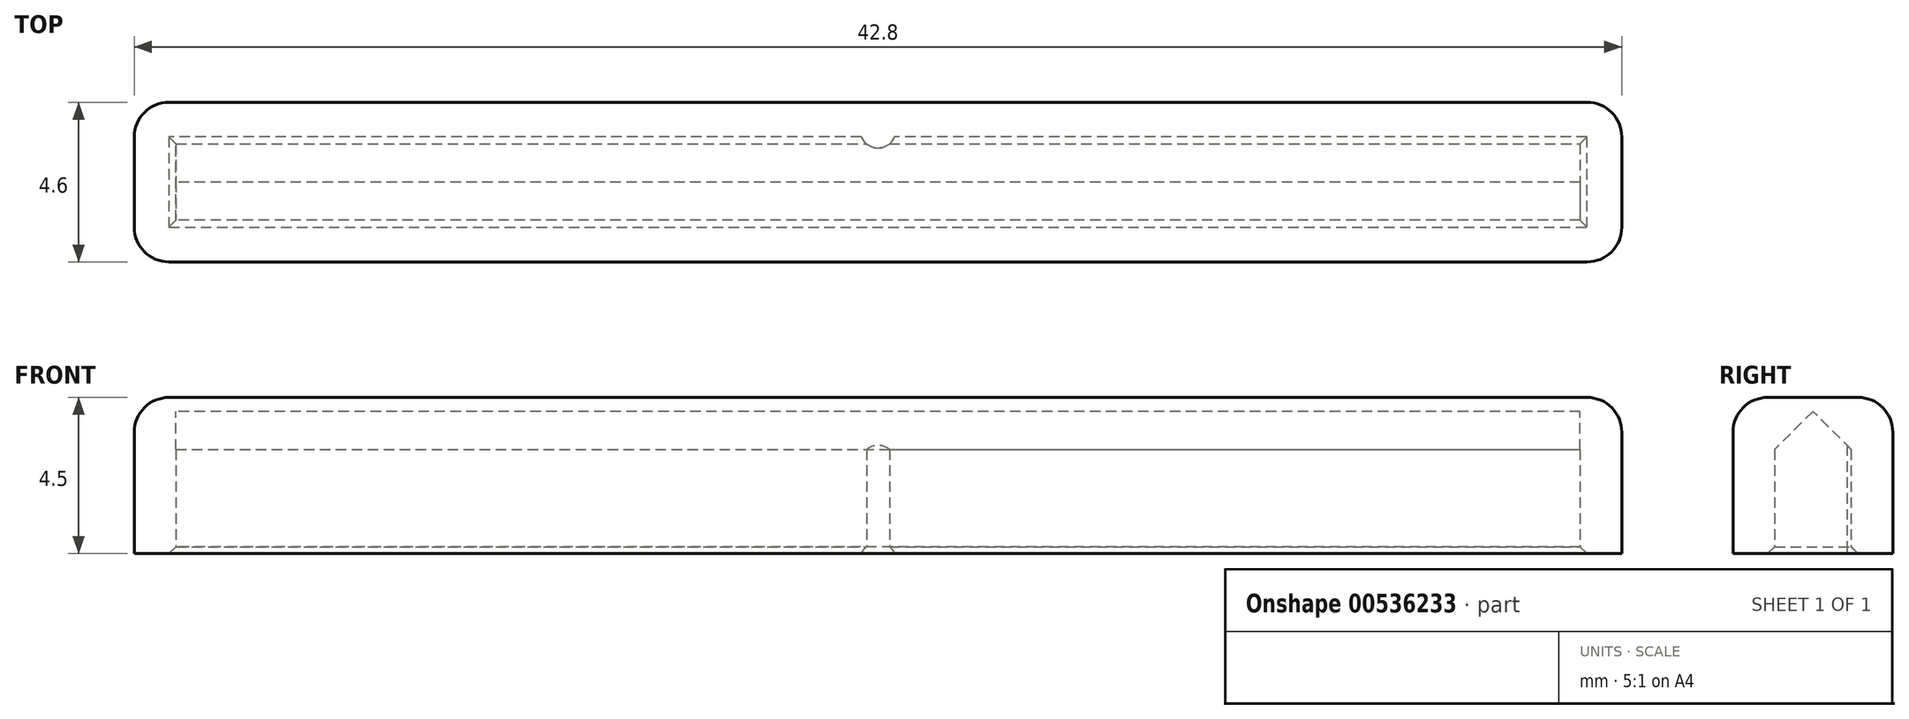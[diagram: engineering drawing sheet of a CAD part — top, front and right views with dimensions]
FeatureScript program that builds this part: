
annotation { "Feature Type Name" : "Feature", "Feature Type Description" : "" }
export const myFeature = defineFeature(function(context is Context, id is Id, definition is map)
    precondition{}
    {
        {
            var Q0;
            Q0=qCreatedBy(makeId("Top.planeOp"),FACE);
            var sketch = newSketch(context, id + "F0", { "sketchPlane" : qUnion([Q0])});
            skLineSegment(sketch, "E0.bottom", {"start": v(-20.2, 1.1) * mm, "end": v(20.2, 1.1) * mm});
            skLineSegment(sketch, "E0.top", {"start": v(-20.2, -1.1) * mm, "end": v(20.2, -1.1) * mm});
            skLineSegment(sketch, "E0.left", {"start": v(-20.2, 1.1) * mm, "end": v(-20.2, -1.1) * mm});
            skLineSegment(sketch, "E0.right", {"start": v(20.2, 1.1) * mm, "end": v(20.2, -1.1) * mm});
            skLineSegment(sketch, "E1.bottom", {"start": v(-21.4, 2.3) * mm, "end": v(21.4, 2.3) * mm});
            skLineSegment(sketch, "E1.top", {"start": v(-21.4, -2.3) * mm, "end": v(21.4, -2.3) * mm});
            skLineSegment(sketch, "E1.left", {"start": v(-21.4, 2.3) * mm, "end": v(-21.4, -2.3) * mm});
            skLineSegment(sketch, "E1.right", {"start": v(21.4, 2.3) * mm, "end": v(21.4, -2.3) * mm});
            skSolve(sketch);
        }
        {
            var Q0;
            Q0 = qSketchRegion(id + "F0", true);
            extrude(context, id + "F1", {"entities" : qUnion([Q0]), "depth" : 3 * mm, "offsetDistance" : 25 * mm});
        }
        {
            var Q0;
            Q0=makeQuery(id+"F1.opExtrude","CAP_FACE",FACE,{"disambiguationData":[OSD([sQuery(id+"F0.wireOp",EDGE,"E0.bottom"),sQuery(id+"F0.wireOp",EDGE,"E0.top"),sQuery(id+"F0.wireOp",EDGE,"E0.left"),sQuery(id+"F0.wireOp",EDGE,"E0.right"),sQuery(id+"F0.wireOp",EDGE,"E1.bottom"),sQuery(id+"F0.wireOp",EDGE,"E1.top"),sQuery(id+"F0.wireOp",EDGE,"E1.left"),sQuery(id+"F0.wireOp",EDGE,"E1.right")])],"isStart":false});
            var sketch = newSketch(context, id + "F2", { "sketchPlane" : qUnion([Q0])});
            skLineSegment(sketch, "E2.bottom", {"start": v(-21.4, 2.3) * mm, "end": v(21.4, 2.3) * mm});
            skLineSegment(sketch, "E2.top", {"start": v(-21.4, -2.3) * mm, "end": v(21.4, -2.3) * mm});
            skLineSegment(sketch, "E2.left", {"start": v(-21.4, 2.3) * mm, "end": v(-21.4, -2.3) * mm});
            skLineSegment(sketch, "E2.right", {"start": v(21.4, 2.3) * mm, "end": v(21.4, -2.3) * mm});
            skSolve(sketch);
        }
        {
            var Q0;
            Q0 = qSketchRegion(id + "F2", true);
            extrude(context, id + "F3", {"entities" : qUnion([Q0]), "operationType" : NewBodyOperationType.ADD, "depth" : 1.5 * mm, "offsetDistance" : 25 * mm});
        }
        {
            var Q0;
            Q0=makeQuery(id+"F1.opExtrude","SWEPT_FACE",FACE,{"disambiguationData":[OSD([sQuery(id+"F0.wireOp",EDGE,"E0.left")])]});
            var sketch = newSketch(context, id + "F4", { "sketchPlane" : qUnion([Q0])});
            skLineSegment(sketch, "E3", {"start": v(1.1, 3) * mm, "end": v(0, 4.1) * mm});
            skLineSegment(sketch, "E4", {"start": v(0, 4.1) * mm, "end": v(-1.1, 3) * mm});
            skLineSegment(sketch, "E5", {"start": v(-1.1, 3) * mm, "end": v(1.1, 3) * mm});
            skSolve(sketch);
        }
        {
            var Q0;
            Q0 = qSketchRegion(id + "F4", true);
            var Q1;
            Q1=makeQuery(id+"F1.opExtrude","SWEPT_FACE",FACE,{"disambiguationData":[OSD([sQuery(id+"F0.wireOp",EDGE,"E0.right")])]});
            extrude(context, id + "F5", {"entities" : qUnion([Q0]), "operationType" : NewBodyOperationType.REMOVE, "endBound" : BoundingType.UP_TO_SURFACE, "depth" : 10 * mm, "endBoundEntityFace" : qUnion([Q1]), "offsetDistance" : 25 * mm});
        }
        {
            var Q0;
            Q0=makeQuery(id+"F1.opExtrude","CAP_EDGE",EDGE,{"disambiguationData":[OSD([sQuery(id+"F0.wireOp",EDGE,"E0.bottom")])],"isStart":true});
            var Q1;
            Q1=makeQuery(id+"F1.opExtrude","CAP_EDGE",EDGE,{"disambiguationData":[OSD([sQuery(id+"F0.wireOp",EDGE,"E0.left")])],"isStart":true});
            var Q2;
            Q2=makeQuery(id+"F1.opExtrude","CAP_EDGE",EDGE,{"disambiguationData":[OSD([sQuery(id+"F0.wireOp",EDGE,"E0.top")])],"isStart":true});
            var Q3;
            Q3=makeQuery(id+"F1.opExtrude","CAP_EDGE",EDGE,{"disambiguationData":[OSD([sQuery(id+"F0.wireOp",EDGE,"E0.right")])],"isStart":true});
            chamfer(context, id + "F6", {"entities" : qUnion([Q0, Q1, Q2, Q3]), "width" : 0.2 * mm, "tangentPropagation" : true});
        }
        {
            var Q0;
            Q0=makeQuery(id+"F3.boolean.opBoolean","MERGE",EDGE,{"derivedFrom":[makeQuery(id+"F1.opExtrude","SWEPT_EDGE",EDGE,{"disambiguationData":[OSD([sQuery(id+"F0.wireOp",EDGE,"E1.top"),sQuery(id+"F0.wireOp",EDGE,"E1.left")])]}),makeQuery(id+"F3.opExtrude","SWEPT_EDGE",EDGE,{"disambiguationData":[OSD([sQuery(id+"F2.wireOp",EDGE,"E2.top"),sQuery(id+"F2.wireOp",EDGE,"E2.left")])]})]});
            var Q1;
            Q1=makeQuery(id+"F3.boolean.opBoolean","MERGE",EDGE,{"derivedFrom":[makeQuery(id+"F1.opExtrude","SWEPT_EDGE",EDGE,{"disambiguationData":[OSD([sQuery(id+"F0.wireOp",EDGE,"E1.bottom"),sQuery(id+"F0.wireOp",EDGE,"E1.left")])]}),makeQuery(id+"F3.opExtrude","SWEPT_EDGE",EDGE,{"disambiguationData":[OSD([sQuery(id+"F2.wireOp",EDGE,"E2.bottom"),sQuery(id+"F2.wireOp",EDGE,"E2.left")])]})]});
            var Q2;
            Q2=makeQuery(id+"F3.opExtrude","CAP_EDGE",EDGE,{"disambiguationData":[OSD([sQuery(id+"F2.wireOp",EDGE,"E2.left")])],"isStart":false});
            var Q3;
            Q3=makeQuery(id+"F3.opExtrude","CAP_EDGE",EDGE,{"disambiguationData":[OSD([sQuery(id+"F2.wireOp",EDGE,"E2.bottom")])],"isStart":false});
            var Q4;
            Q4=makeQuery(id+"F3.opExtrude","CAP_EDGE",EDGE,{"disambiguationData":[OSD([sQuery(id+"F2.wireOp",EDGE,"E2.top")])],"isStart":false});
            var Q5;
            Q5=makeQuery(id+"F3.boolean.opBoolean","MERGE",EDGE,{"derivedFrom":[makeQuery(id+"F1.opExtrude","SWEPT_EDGE",EDGE,{"disambiguationData":[OSD([sQuery(id+"F0.wireOp",EDGE,"E1.top"),sQuery(id+"F0.wireOp",EDGE,"E1.right")])]}),makeQuery(id+"F3.opExtrude","SWEPT_EDGE",EDGE,{"disambiguationData":[OSD([sQuery(id+"F2.wireOp",EDGE,"E2.top"),sQuery(id+"F2.wireOp",EDGE,"E2.right")])]})]});
            var Q6;
            Q6=makeQuery(id+"F3.opExtrude","CAP_EDGE",EDGE,{"disambiguationData":[OSD([sQuery(id+"F2.wireOp",EDGE,"E2.right")])],"isStart":false});
            var Q7;
            Q7=makeQuery(id+"F3.boolean.opBoolean","MERGE",EDGE,{"derivedFrom":[makeQuery(id+"F1.opExtrude","SWEPT_EDGE",EDGE,{"disambiguationData":[OSD([sQuery(id+"F0.wireOp",EDGE,"E1.bottom"),sQuery(id+"F0.wireOp",EDGE,"E1.right")])]}),makeQuery(id+"F3.opExtrude","SWEPT_EDGE",EDGE,{"disambiguationData":[OSD([sQuery(id+"F2.wireOp",EDGE,"E2.bottom"),sQuery(id+"F2.wireOp",EDGE,"E2.right")])]})]});
            fillet(context, id + "F7", {"entities" : qUnion([Q0, Q1, Q2, Q3, Q4, Q5, Q6, Q7]), "radius" : 1 * mm, "tangentPropagation" : true, "allowEdgeOverflow" : false});
        }
        {
            var Q0;
            Q0=makeQuery(id+"F1.opExtrude","CAP_FACE",FACE,{"disambiguationData":[OSD([sQuery(id+"F0.wireOp",EDGE,"E0.bottom"),sQuery(id+"F0.wireOp",EDGE,"E0.top"),sQuery(id+"F0.wireOp",EDGE,"E0.left"),sQuery(id+"F0.wireOp",EDGE,"E0.right"),sQuery(id+"F0.wireOp",EDGE,"E1.bottom"),sQuery(id+"F0.wireOp",EDGE,"E1.top"),sQuery(id+"F0.wireOp",EDGE,"E1.left"),sQuery(id+"F0.wireOp",EDGE,"E1.right")])],"isStart":true});
            var sketch = newSketch(context, id + "F8", { "sketchPlane" : qUnion([Q0])});
            skArc(sketch, "E6", {"start": v(0.48, -1.3) * mm, "mid": v(0, -0.98) * mm, "end": v(-0.48, -1.3) * mm});
            skPoint(sketch, "E7", {"position": v(0, -1.3) * mm});
            skLineSegment(sketch, "E8", {"start": v(-0.48, -1.3) * mm, "end": v(0.48, -1.3) * mm});
            skSolve(sketch);
        }
        {
            var Q0;
            Q0 = qSketchRegion(id + "F8", true);
            var Q1;
            Q1=makeQuery(id+"F5.boolean.opBoolean","COPY",FACE,{"derivedFrom":makeQuery(id+"F5.opExtrude","SWEPT_FACE",FACE,{"disambiguationData":[OSD([sQuery(id+"F4.wireOp",EDGE,"E3")])]})});
            extrude(context, id + "F9", {"entities" : qUnion([Q0]), "operationType" : NewBodyOperationType.ADD, "endBound" : BoundingType.UP_TO_SURFACE, "oppositeDirection" : true, "depth" : 25 * mm, "endBoundEntityFace" : qUnion([Q1]), "offsetDistance" : 25 * mm});
        }
    });
